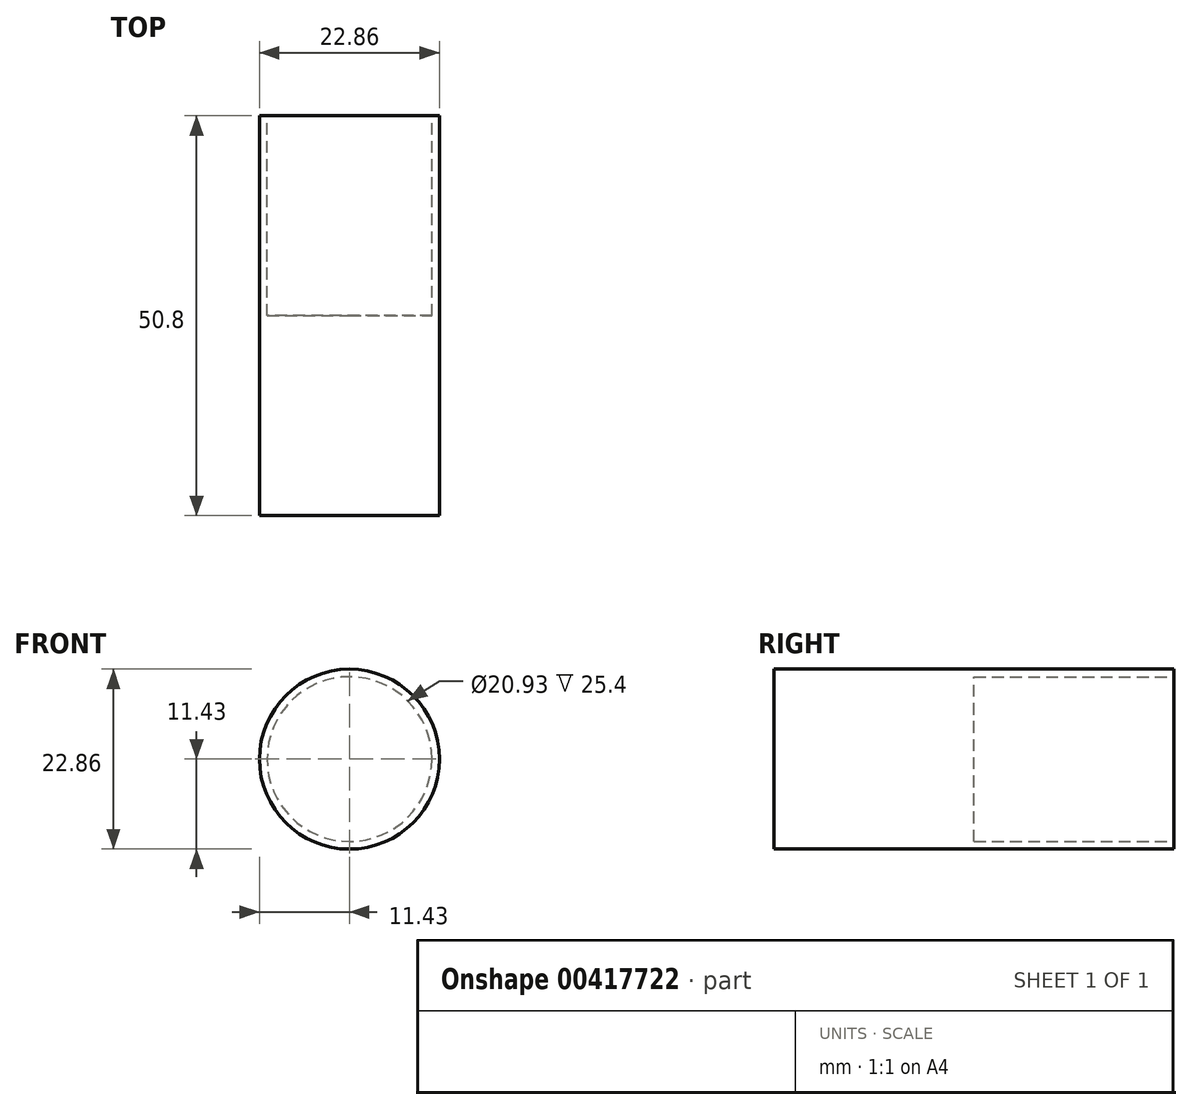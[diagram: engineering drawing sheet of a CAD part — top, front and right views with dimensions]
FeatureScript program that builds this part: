
annotation { "Feature Type Name" : "Feature", "Feature Type Description" : "" }
export const myFeature = defineFeature(function(context is Context, id is Id, definition is map)
    precondition{}
    {
        {
            var Q0;
            Q0=qCreatedBy(makeId("Front.planeOp"),FACE);
            var sketch = newSketch(context, id + "F0", { "sketchPlane" : qUnion([Q0])});
            skCircle(sketch, "E0", {"center": v(0, 0) * mm, "radius": 11.43 * mm});
            skCircle(sketch, "E1", {"center": v(0, 0) * mm, "radius": 10.46 * mm});
            skSolve(sketch);
        }
        {
            var Q0;
            Q0=makeQuery(id+"F0.imprint","IMPRINT",FACE,{"disambiguationData":[TD([[makeQuery(id+"F0.imprint","IMPRINT",EDGE,{"derivedFrom":sQuery(id+"F0.wireOp",EDGE,"E0")}),1.0]])]});
            extrude(context, id + "F1", {"entities" : qUnion([Q0]), "endBound" : BoundingType.SYMMETRIC, "depth" : 50.8 * mm});
        }
        {
            var Q0;
            Q0=qCreatedBy(makeId("Front.planeOp"),FACE);
            var sketch = newSketch(context, id + "F2", { "sketchPlane" : qUnion([Q0])});
            skCircle(sketch, "E2", {"center": v(0, 0) * mm, "radius": 10.46 * mm});
            skSolve(sketch);
        }
        {
            var Q0;
            Q0 = qSketchRegion(id + "F2", true);
            var Q1;
            Q1=makeQuery(id+"F1.opExtrude","CAP_FACE",FACE,{"disambiguationData":[OSD([sQuery(id+"F0.wireOp",EDGE,"E0"),sQuery(id+"F0.wireOp",EDGE,"E1")])],"isStart":false});
            extrude(context, id + "F3", {"entities" : qUnion([Q0]), "operationType" : NewBodyOperationType.ADD, "endBound" : BoundingType.UP_TO_SURFACE, "endBoundEntityFace" : qUnion([Q1]), "depth" : 112.52 * mm});
        }
    });
